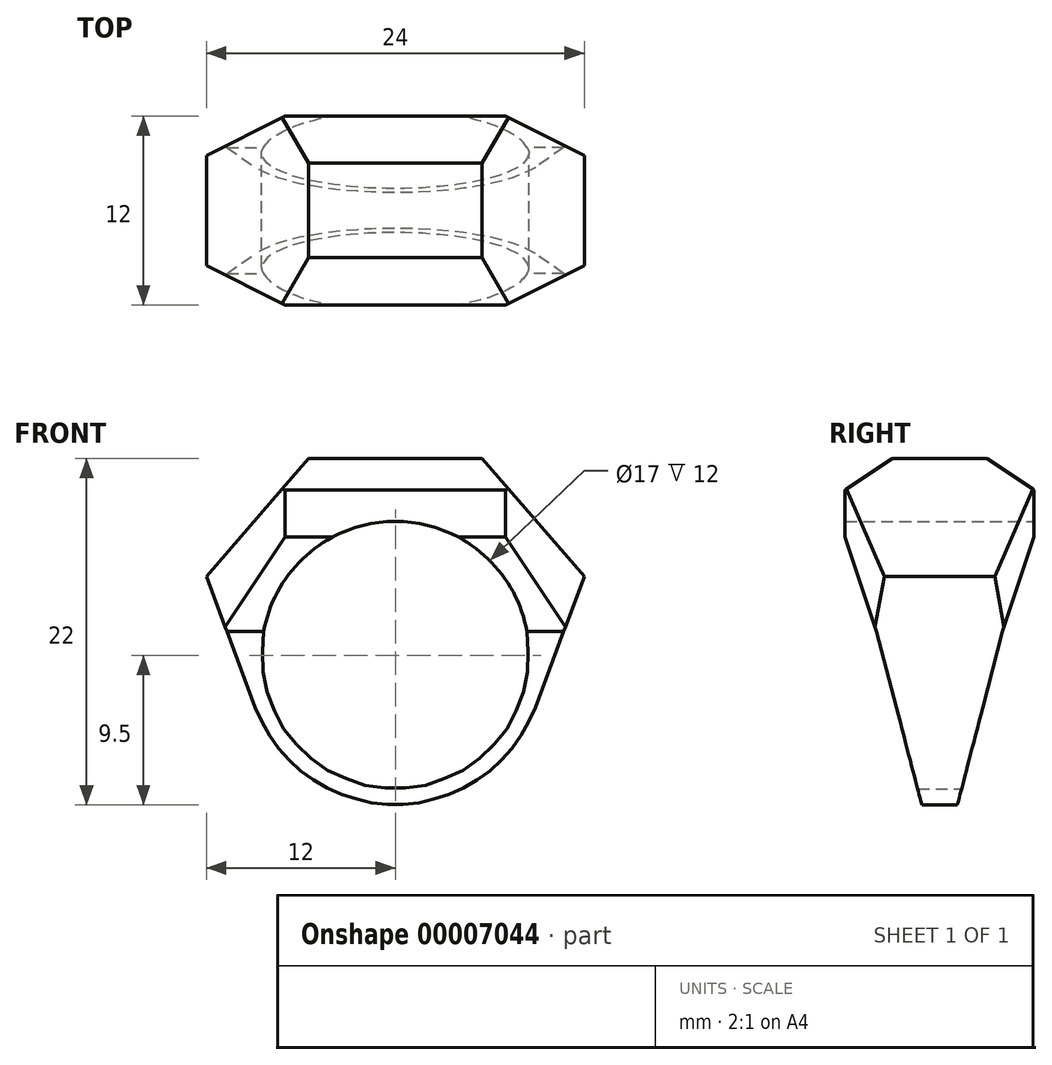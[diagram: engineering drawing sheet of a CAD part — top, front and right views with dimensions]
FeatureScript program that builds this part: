
annotation { "Feature Type Name" : "Feature", "Feature Type Description" : "" }
export const myFeature = defineFeature(function(context is Context, id is Id, definition is map)
    precondition{}
    {
        {
            var Q0;
            Q0=qCreatedBy(makeId("Front.planeOp"),FACE);
            var sketch = newSketch(context, id + "F0", { "sketchPlane" : qUnion([Q0])});
            skCircle(sketch, "E0", {"center": v(0, 0) * mm, "radius": 8.5 * mm});
            skArc(sketch, "E1", {"start": v(-8.9, 3.3) * mm, "mid": v(0, -9.5) * mm, "end": v(8.9, 3.3) * mm});
            skLineSegment(sketch, "E2", {"start": v(-5.5, 12.5) * mm, "end": v(5.5, 12.5) * mm});
            skLineSegment(sketch, "E3", {"start": v(5.5, 12.5) * mm, "end": v(8.9, 3.3) * mm});
            skLineSegment(sketch, "E4", {"start": v(-5.5, 12.5) * mm, "end": v(-8.9, 3.3) * mm});
            skPoint(sketch, "E5", {"position": v(0, 12.5) * mm});
            skLineSegment(sketch, "E6", {"start": v(-8.9, -3.32) * mm, "end": v(-12, 5) * mm});
            skLineSegment(sketch, "E7", {"start": v(-12, 5) * mm, "end": v(-5.5, 12.5) * mm});
            skLineSegment(sketch, "E8", {"start": v(5.5, 12.5) * mm, "end": v(12, 5) * mm});
            skLineSegment(sketch, "E9", {"start": v(12, 5) * mm, "end": v(8.9, -3.32) * mm});
            skLineSegment(sketch, "E10", {"start": v(-12, 5) * mm, "end": v(12, 5) * mm});
            skPoint(sketch, "E11", {"position": v(0, 5) * mm});
            skSolve(sketch);
        }
        {
            var Q0;
            Q0 = qSketchRegion(id + "F0", true);
            extrude(context, id + "F1", {"entities" : qUnion([Q0]), "endBound" : BoundingType.SYMMETRIC, "depth" : 12 * mm});
        }
        {
            var Q0;
            Q0=qCreatedBy(makeId("Right.planeOp"),FACE);
            var sketch = newSketch(context, id + "F2", { "sketchPlane" : qUnion([Q0])});
            skLineSegment(sketch, "E12", {"start": v(-1, -10) * mm, "end": v(-4, 1.5) * mm});
            skLineSegment(sketch, "E13", {"start": v(-4, 1.5) * mm, "end": v(-6, 7.5) * mm});
            skLineSegment(sketch, "E14", {"start": v(-6, 7.5) * mm, "end": v(-6, 10.5) * mm});
            skLineSegment(sketch, "E15", {"start": v(-1, -10) * mm, "end": v(1, -10) * mm});
            skLineSegment(sketch, "E16", {"start": v(1, -10) * mm, "end": v(4, 1.5) * mm});
            skLineSegment(sketch, "E17", {"start": v(4, 1.5) * mm, "end": v(6, 7.5) * mm});
            skLineSegment(sketch, "E18", {"start": v(6, 7.5) * mm, "end": v(6, 10.5) * mm});
            skLineSegment(sketch, "E19", {"start": v(3, 12.5) * mm, "end": v(-3, 12.5) * mm});
            skPoint(sketch, "E20", {"position": v(0, 12.5) * mm});
            skPoint(sketch, "E21", {"position": v(0, -10) * mm});
            skLineSegment(sketch, "E22.bottom", {"start": v(-11.26, 21.2) * mm, "end": v(15.8, 21.2) * mm});
            skLineSegment(sketch, "E22.top", {"start": v(-11.26, -22.88) * mm, "end": v(15.8, -22.88) * mm});
            skLineSegment(sketch, "E22.left", {"start": v(-11.26, 21.2) * mm, "end": v(-11.26, -22.88) * mm});
            skLineSegment(sketch, "E22.right", {"start": v(15.8, 21.2) * mm, "end": v(15.8, -22.88) * mm});
            skLineSegment(sketch, "E23", {"start": v(-6, 10.5) * mm, "end": v(-3, 12.5) * mm});
            skLineSegment(sketch, "E24", {"start": v(6, 10.5) * mm, "end": v(3, 12.5) * mm});
            skPoint(sketch, "E25.orphan", {"position": v(-6, 12.5) * mm});
            skPoint(sketch, "E26.orphan", {"position": v(6, 12.5) * mm});
            skSolve(sketch);
        }
        {
            var Q0;
            Q0=makeQuery(id+"F2.imprint","IMPRINT",FACE,{"disambiguationData":[TD([[makeQuery(id+"F2.imprint","IMPRINT",EDGE,{"derivedFrom":sQuery(id+"F2.wireOp",EDGE,"E12")}),1.0]])]});
            extrude(context, id + "F3", {"entities" : qUnion([Q0]), "operationType" : NewBodyOperationType.REMOVE, "endBound" : BoundingType.THROUGH_ALL, "oppositeDirection" : true, "depth" : 25 * mm});
        }
        {
            var Q0;
            Q0 = qSketchRegion(id + "F2", true);
            extrude(context, id + "F4", {"entities" : qUnion([Q0]), "operationType" : NewBodyOperationType.REMOVE, "endBound" : BoundingType.THROUGH_ALL, "depth" : 25 * mm});
        }
        {
            var Q0;
            Q0=makeQuery(id+"F1.opExtrude","SWEPT_FACE",FACE,{"disambiguationData":[OSD([sQuery(id+"F0.wireOp",EDGE,"E2")])]});
            var sketch = newSketch(context, id + "F5", { "sketchPlane" : qUnion([Q0])});
            skLineSegment(sketch, "E27.bottom", {"start": v(14.49, -13.98) * mm, "end": v(-18.59, -13.98) * mm});
            skLineSegment(sketch, "E27.top", {"start": v(14.49, 16.9) * mm, "end": v(-18.59, 16.9) * mm});
            skLineSegment(sketch, "E27.left", {"start": v(14.49, -13.98) * mm, "end": v(14.49, 16.9) * mm});
            skLineSegment(sketch, "E27.right", {"start": v(-18.59, -13.98) * mm, "end": v(-18.59, 16.9) * mm});
            skLineSegment(sketch, "E28", {"start": v(-12, -3.5) * mm, "end": v(-7, -6) * mm});
            skLineSegment(sketch, "E29", {"start": v(-7, -6) * mm, "end": v(7, -6) * mm});
            skLineSegment(sketch, "E30", {"start": v(7, -6) * mm, "end": v(12, -3.5) * mm});
            skLineSegment(sketch, "E31", {"start": v(12, -3.5) * mm, "end": v(12, 3.5) * mm});
            skLineSegment(sketch, "E32", {"start": v(12, 3.5) * mm, "end": v(7, 6) * mm});
            skLineSegment(sketch, "E33", {"start": v(7, 6) * mm, "end": v(-7, 6) * mm});
            skLineSegment(sketch, "E34", {"start": v(-7, 6) * mm, "end": v(-12, 3.5) * mm});
            skLineSegment(sketch, "E35", {"start": v(-12, 3.5) * mm, "end": v(-12, -3.5) * mm});
            skPoint(sketch, "E36", {"position": v(0, -6) * mm});
            skPoint(sketch, "E37", {"position": v(0, 6) * mm});
            skPoint(sketch, "E38", {"position": v(-12, 0) * mm});
            skPoint(sketch, "E39", {"position": v(12, 0) * mm});
            skSolve(sketch);
        }
        {
            var Q0;
            Q0 = qSketchRegion(id + "F5", true);
            extrude(context, id + "F6", {"entities" : qUnion([Q0]), "operationType" : NewBodyOperationType.REMOVE, "endBound" : BoundingType.THROUGH_ALL, "oppositeDirection" : true, "depth" : 25 * mm});
        }
    });
